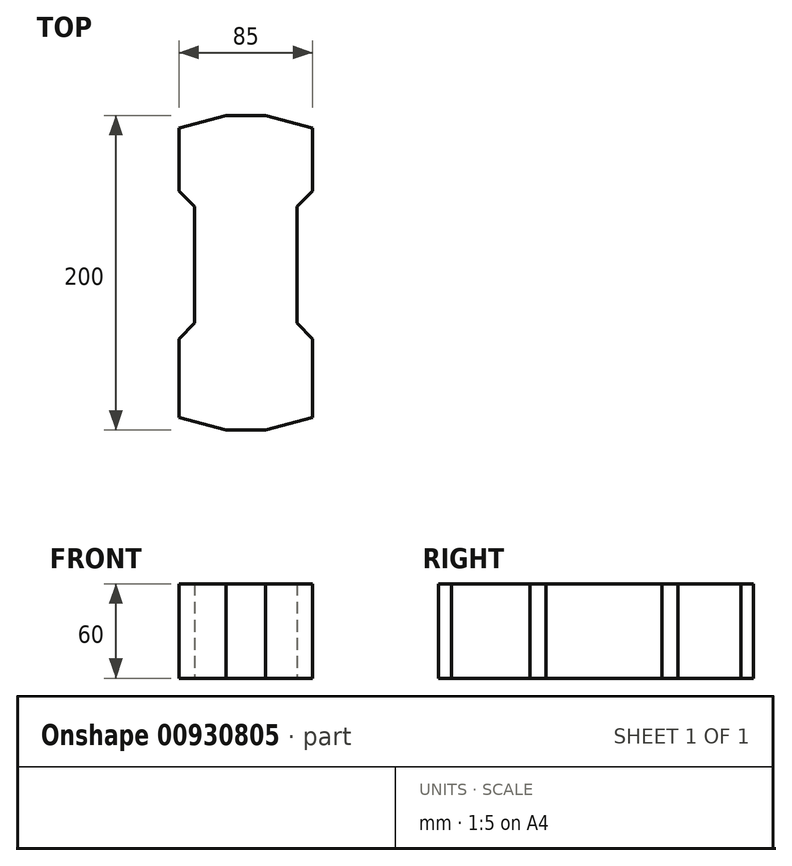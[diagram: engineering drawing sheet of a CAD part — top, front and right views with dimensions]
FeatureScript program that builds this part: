
annotation { "Feature Type Name" : "Feature", "Feature Type Description" : "" }
export const myFeature = defineFeature(function(context is Context, id is Id, definition is map)
    precondition{}
    {
        {
            var Q0;
            Q0=qCreatedBy(makeId("Top.planeOp"),FACE);
            var sketch = newSketch(context, id + "F0", { "sketchPlane" : qUnion([Q0])});
            skLineSegment(sketch, "E0.bottom", {"start": v(-137.5, 110) * mm, "end": v(137.5, 110) * mm, "construction": true});
            skLineSegment(sketch, "E0.top", {"start": v(-137.5, -110) * mm, "end": v(137.5, -110) * mm, "construction": true});
            skLineSegment(sketch, "E0.left", {"start": v(-137.5, 110) * mm, "end": v(-137.5, -110) * mm, "construction": true});
            skLineSegment(sketch, "E0.right", {"start": v(137.5, 110) * mm, "end": v(137.5, -110) * mm, "construction": true});
            skPoint(sketch, "E0.middle", {"position": v(0, 0) * mm});
            skCircle(sketch, "E1", {"center": v(-137.5, 110) * mm, "radius": 105 * mm, "construction": true});
            skCircle(sketch, "E2", {"center": v(-137.5, -110) * mm, "radius": 105 * mm, "construction": true});
            skCircle(sketch, "E3", {"center": v(137.5, -110) * mm, "radius": 105 * mm, "construction": true});
            skCircle(sketch, "E4", {"center": v(137.5, 110) * mm, "radius": 105 * mm, "construction": true});
            skLineSegment(sketch, "E5.bottom", {"start": v(42.5, -100) * mm, "end": v(-42.5, -100) * mm});
            skLineSegment(sketch, "E5.top", {"start": v(42.5, 100) * mm, "end": v(-42.5, 100) * mm});
            skLineSegment(sketch, "E5.left", {"start": v(42.5, -100) * mm, "end": v(42.5, 100) * mm});
            skLineSegment(sketch, "E5.right", {"start": v(-42.5, -100) * mm, "end": v(-42.5, 100) * mm});
            skLineSegment(sketch, "E6", {"start": v(-12.5, -100) * mm, "end": v(-42.5, -91.96) * mm});
            skLineSegment(sketch, "E7", {"start": v(-42.5, -41.96) * mm, "end": v(-32.5, -31.96) * mm});
            skLineSegment(sketch, "E8", {"start": v(-32.5, -31.96) * mm, "end": v(-32.5, 41.96) * mm});
            skLineSegment(sketch, "E9", {"start": v(-32.5, 41.96) * mm, "end": v(-42.5, 51.96) * mm});
            skLineSegment(sketch, "E10", {"start": v(-42.5, 51.96) * mm, "end": v(-42.5, 91.96) * mm});
            skLineSegment(sketch, "E11", {"start": v(-42.5, 91.96) * mm, "end": v(-12.5, 100) * mm});
            skLineSegment(sketch, "E12.MirrorCS", {"start": v(12.5, -100) * mm, "end": v(42.5, -91.96) * mm});
            skLineSegment(sketch, "E13.MirrorCS", {"start": v(42.5, -41.96) * mm, "end": v(32.5, -31.96) * mm});
            skLineSegment(sketch, "E14.MirrorCS", {"start": v(32.5, -31.96) * mm, "end": v(32.5, 41.96) * mm});
            skLineSegment(sketch, "E15.MirrorCS", {"start": v(32.5, 41.96) * mm, "end": v(42.5, 51.96) * mm});
            skLineSegment(sketch, "E16.MirrorCS", {"start": v(42.5, 91.96) * mm, "end": v(12.5, 100) * mm});
            skSolve(sketch);
        }
        {
            var Q0;
            {var subQ1=sQuery(id+"F0.wireOp",EDGE,"E6");Q0=makeQuery(id+"F0.imprint","IMPRINT",FACE,{"disambiguationData":[TD([[makeQuery(id+"F0.imprint","IMPRINT",EDGE,{"derivedFrom":subQ1}),-1.0]])]});}
            extrude(context, id + "F1", {"entities" : qUnion([Q0]), "depth" : 60 * mm, "offsetDistance" : 25 * mm});
        }
    });
